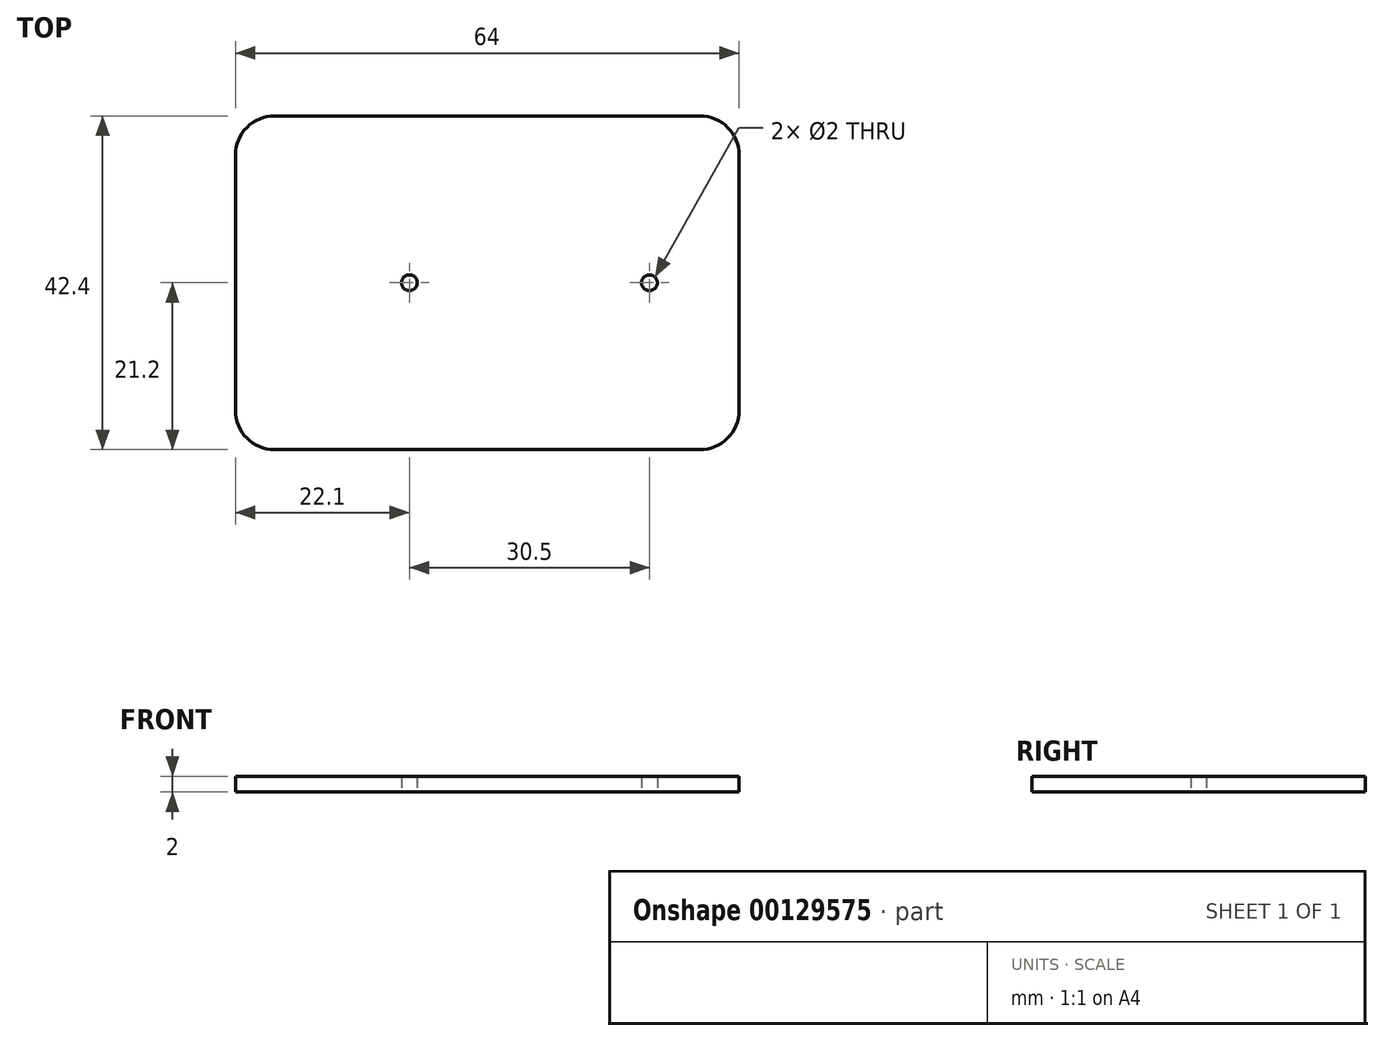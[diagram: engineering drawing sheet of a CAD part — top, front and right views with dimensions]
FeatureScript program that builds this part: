
annotation { "Feature Type Name" : "Feature", "Feature Type Description" : "" }
export const myFeature = defineFeature(function(context is Context, id is Id, definition is map)
    precondition{}
    {
        {
            var Q0;
            Q0=qCreatedBy(makeId("Top.planeOp"),FACE);
            var sketch = newSketch(context, id + "F0", { "sketchPlane" : qUnion([Q0])});
            skLineSegment(sketch, "E0.bottom", {"start": v(-32, 21.2) * mm, "end": v(32, 21.2) * mm});
            skLineSegment(sketch, "E0.top", {"start": v(-32, -21.2) * mm, "end": v(32, -21.2) * mm});
            skLineSegment(sketch, "E0.left", {"start": v(-32, 21.2) * mm, "end": v(-32, -21.2) * mm});
            skLineSegment(sketch, "E0.right", {"start": v(32, 21.2) * mm, "end": v(32, -21.2) * mm});
            skCircle(sketch, "E1", {"center": v(20.6, 0) * mm, "radius": 1 * mm});
            skCircle(sketch, "E2", {"center": v(-9.9, 0) * mm, "radius": 1 * mm});
            skSolve(sketch);
        }
        {
            var Q0;
            Q0 = qSketchRegion(id + "F0", true);
            var Q1;
            Q1=makeQuery(id+"F0.imprint","IMPRINT",FACE,{"disambiguationData":[TD([[makeQuery(id+"F0.imprint","IMPRINT",EDGE,{"derivedFrom":sQuery(id+"F0.wireOp",EDGE,"E0.bottom")}),-1.0]])]});
            extrude(context, id + "F1", {"entities" : qUnion([Q0, Q1]), "depth" : 2 * mm});
        }
        {
            var Q0;
            Q0=makeQuery(id+"F1.opExtrude","SWEPT_EDGE",EDGE,{"disambiguationData":[OSD([sQuery(id+"F0.wireOp",EDGE,"E0.top"),sQuery(id+"F0.wireOp",EDGE,"E0.right")])]});
            var Q1;
            Q1=makeQuery(id+"F1.opExtrude","SWEPT_EDGE",EDGE,{"disambiguationData":[OSD([sQuery(id+"F0.wireOp",EDGE,"E0.bottom"),sQuery(id+"F0.wireOp",EDGE,"E0.right")])]});
            var Q2;
            Q2=makeQuery(id+"F1.opExtrude","SWEPT_EDGE",EDGE,{"disambiguationData":[OSD([sQuery(id+"F0.wireOp",EDGE,"E0.bottom"),sQuery(id+"F0.wireOp",EDGE,"E0.left")])]});
            var Q3;
            Q3=makeQuery(id+"F1.opExtrude","SWEPT_EDGE",EDGE,{"disambiguationData":[OSD([sQuery(id+"F0.wireOp",EDGE,"E0.top"),sQuery(id+"F0.wireOp",EDGE,"E0.left")])]});
            fillet(context, id + "F2", {"entities" : qUnion([Q0, Q1, Q2, Q3]), "radius" : 5 * mm, "tangentPropagation" : true, "allowEdgeOverflow" : false});
        }
    });
